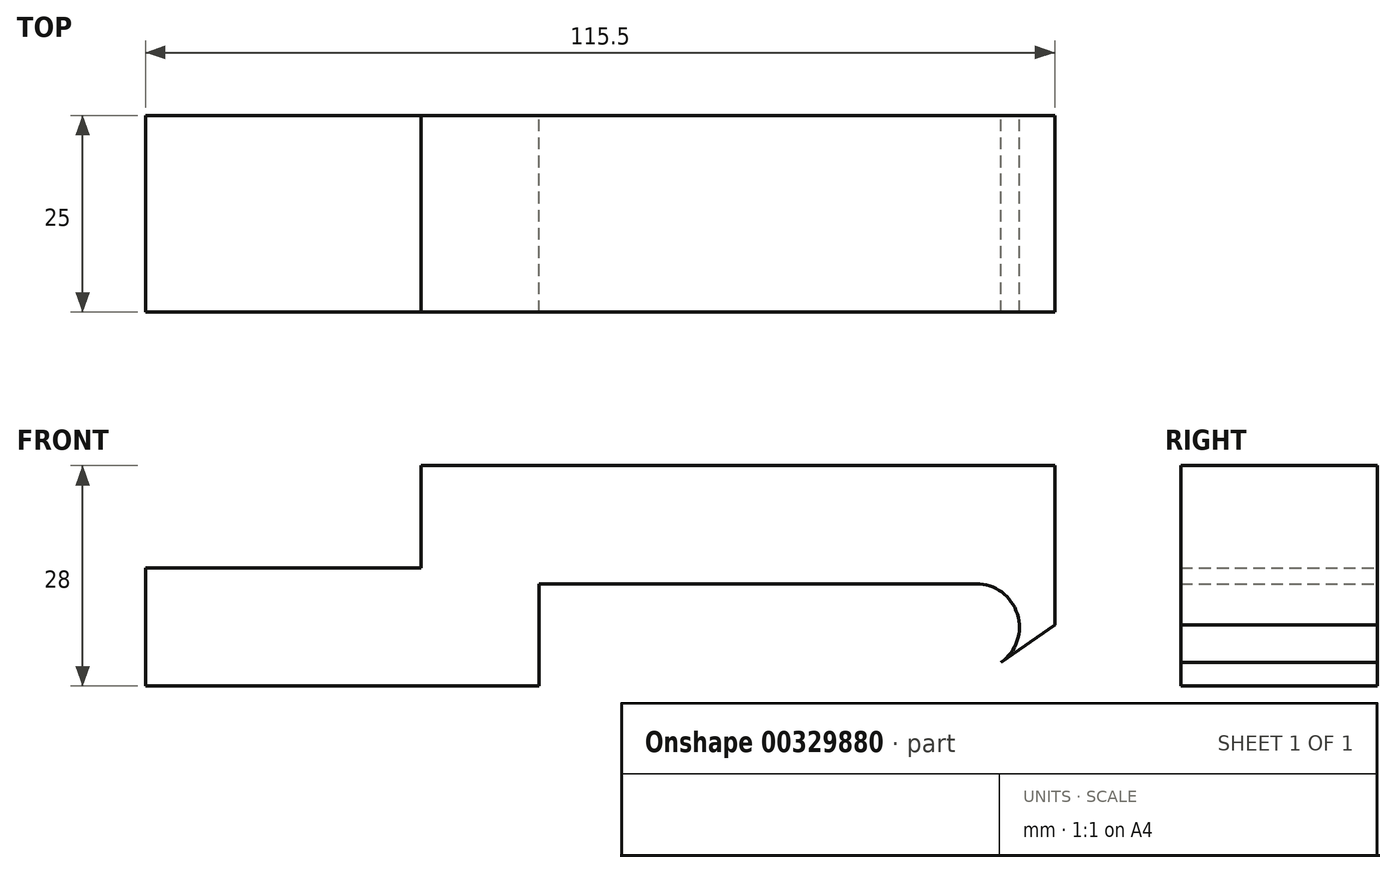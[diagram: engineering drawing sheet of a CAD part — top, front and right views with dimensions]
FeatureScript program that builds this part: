
annotation { "Feature Type Name" : "Feature", "Feature Type Description" : "" }
export const myFeature = defineFeature(function(context is Context, id is Id, definition is map)
    precondition{}
    {
        {
            var Q0;
            Q0=qCreatedBy(makeId("Front.planeOp"),FACE);
            var sketch = newSketch(context, id + "F0", { "sketchPlane" : qUnion([Q0])});
            skLineSegment(sketch, "E0", {"start": v(-50, 0) * mm, "end": v(0, 0) * mm});
            skLineSegment(sketch, "E1", {"start": v(0, 0) * mm, "end": v(0, 13) * mm});
            skLineSegment(sketch, "E2", {"start": v(0, 13) * mm, "end": v(55.5, 13) * mm});
            skArc(sketch, "E3", {"start": v(58.65, 3) * mm, "mid": v(60.75, 9.15) * mm, "end": v(55.5, 13) * mm});
            skLineSegment(sketch, "E4", {"start": v(58.65, 3) * mm, "end": v(65.5, 7.79) * mm});
            skLineSegment(sketch, "E5", {"start": v(65.5, 7.79) * mm, "end": v(65.5, 28) * mm});
            skLineSegment(sketch, "E6", {"start": v(65.5, 28) * mm, "end": v(-15, 28) * mm});
            skLineSegment(sketch, "E7", {"start": v(-15, 28) * mm, "end": v(-15, 15) * mm});
            skLineSegment(sketch, "E8", {"start": v(-15, 15) * mm, "end": v(-50, 15) * mm});
            skLineSegment(sketch, "E9", {"start": v(-50, 15) * mm, "end": v(-50, 0) * mm});
            skArc(sketch, "E10", {"start": v(55.5, 13) * mm, "mid": v(50.25, 5.85) * mm, "end": v(58.65, 3) * mm, "construction": true});
            skLineSegment(sketch, "E11", {"start": v(55.5, 13) * mm, "end": v(55.5, 7.5) * mm, "construction": true});
            skLineSegment(sketch, "E12", {"start": v(55.5, 7.5) * mm, "end": v(58.65, 3) * mm, "construction": true});
            skSolve(sketch);
        }
        {
            var Q0;
            Q0 = qSketchRegion(id + "F0", true);
            extrude(context, id + "F1", {"entities" : qUnion([Q0]), "depth" : 25 * mm, "offsetDistance" : 25 * mm});
        }
    });
